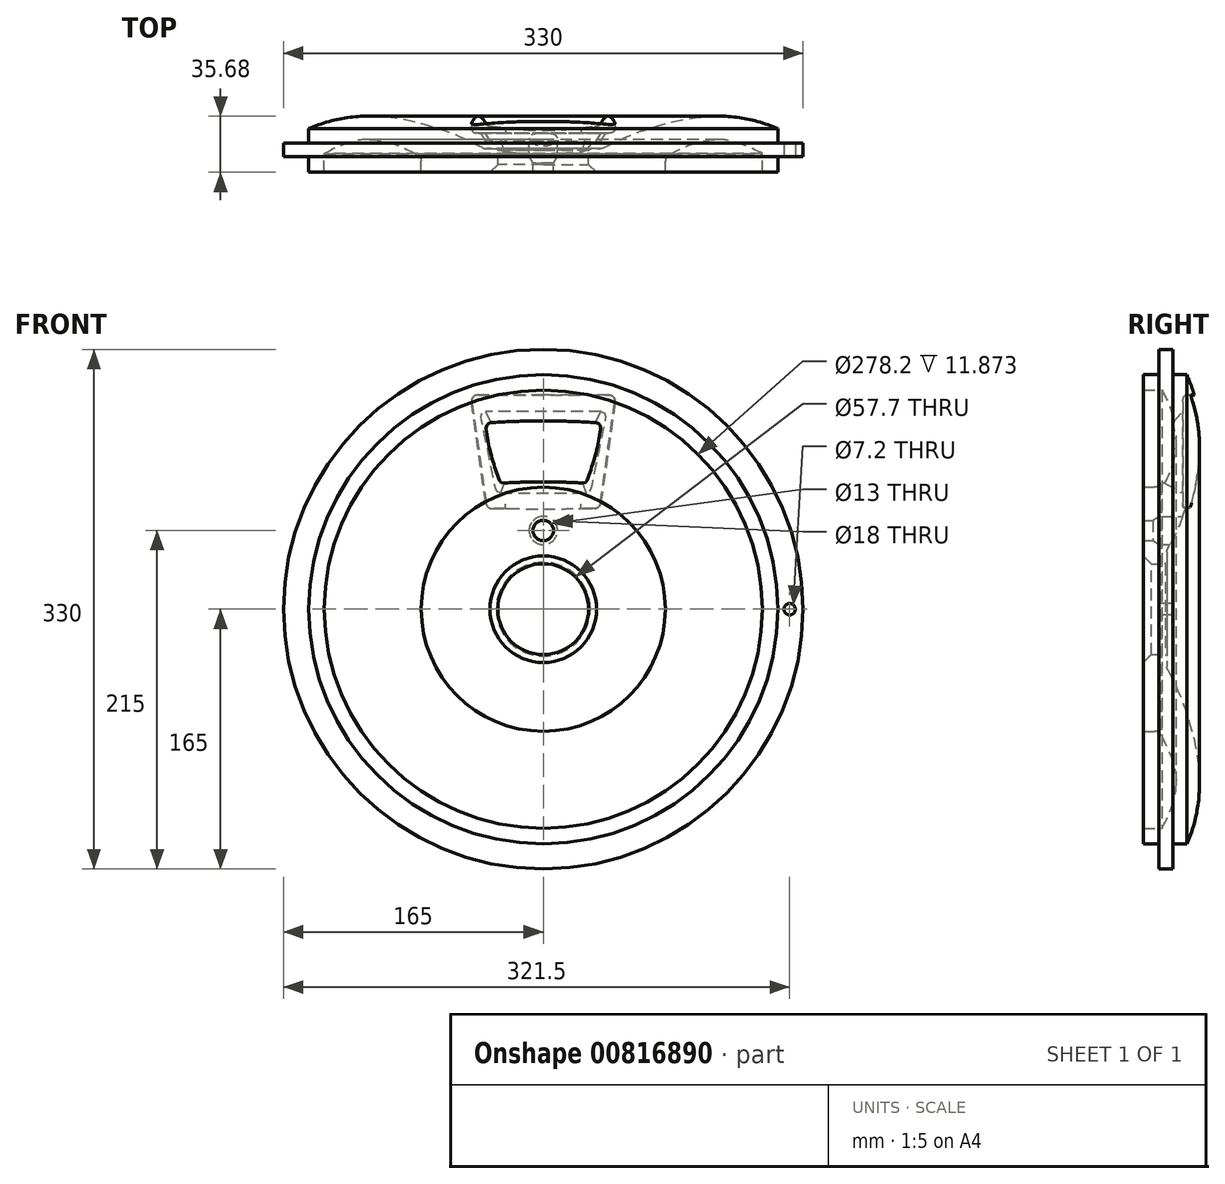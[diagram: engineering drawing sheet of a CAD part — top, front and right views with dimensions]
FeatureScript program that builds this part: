
annotation { "Feature Type Name" : "Feature", "Feature Type Description" : "" }
export const myFeature = defineFeature(function(context is Context, id is Id, definition is map)
    precondition{}
    {
        {
            var Q0;
            Q0=qCreatedBy(makeId("Top.planeOp"),FACE);
            var sketch = newSketch(context, id + "F0", { "sketchPlane" : qUnion([Q0])});
            skLineSegment(sketch, "E0", {"start": v(-28.85, 0) * mm, "end": v(-28.85, 15) * mm});
            skLineSegment(sketch, "E1", {"start": v(-28.85, 15) * mm, "end": v(-36.25, 15) * mm});
            skFitSpline(sketch, "E2", {"points": [v(-37.5, 15) * mm, v(-69.56, 28.6) * mm, v(-105.66, 35.55) * mm, v(-165, 18.67) * mm], "startDerivative": vector(-135.79, 72.9) * mm, "endDerivative": vector(-162.08, -109.99) * mm});
            skLineSegment(sketch, "E3", {"start": v(-165, 10) * mm, "end": v(-149, 10) * mm});
            skLineSegment(sketch, "E4", {"start": v(-149, 10) * mm, "end": v(-149, 0) * mm});
            skLineSegment(sketch, "E5", {"start": v(-149, 0) * mm, "end": v(-139.1, 0) * mm});
            skLineSegment(sketch, "E6", {"start": v(-139.1, 0) * mm, "end": v(-139.1, 11.87) * mm});
            skLineSegment(sketch, "E7", {"start": v(-77.5, 7) * mm, "end": v(-77.5, 0) * mm});
            skLineSegment(sketch, "E8", {"start": v(-77.5, 0) * mm, "end": v(-28.85, 0) * mm});
            skLineSegment(sketch, "E9", {"start": v(0, 47.35) * mm, "end": v(0, -31.33) * mm, "construction": true});
            skFitSpline(sketch, "E10", {"points": [v(-139.1, 11.87) * mm, v(-77.5, 10) * mm], "startDerivative": vector(71.54, 38.93) * mm, "endDerivative": vector(74.78, -40.54) * mm});
            skLineSegment(sketch, "E11", {"start": v(-165, 18.67) * mm, "end": v(-149, 18.67) * mm});
            skLineSegment(sketch, "E12", {"start": v(-149, 18.67) * mm, "end": v(-149, 27.64) * mm});
            skLineSegment(sketch, "E13", {"start": v(-165, 18.67) * mm, "end": v(-165, 10) * mm});
            skArc(sketch, "E14.filletArc", {"start": v(-77.5, 7) * mm, "mid": v(-78.22, 9.59) * mm, "end": v(-80.18, 11.43) * mm});
            skArc(sketch, "E15.filletArc", {"start": v(-38.6, 15.58) * mm, "mid": v(-37.46, 15.15) * mm, "end": v(-36.25, 15) * mm});
            skSolve(sketch);
        }
        {
            var Q0;
            Q0=makeQuery(id+"F0.imprint","IMPRINT",FACE,{"disambiguationData":[TD([[makeQuery(id+"F0.imprint","IMPRINT",EDGE,{"derivedFrom":sQuery(id+"F0.wireOp",EDGE,"E0")}),1.0]])]});
            var Q1;
            Q1=sQuery(id+"F0.wireOp",EDGE,"E9");
            revolve(context, id + "F1", {"surfaceOperationType" : NewSurfaceOperationType.NEW, "entities" : qUnion([Q0]), "axis" : qUnion([Q1]), "revolveType" : RevolveType.FULL});
        }
        {
            var Q0;
            Q0=qCreatedBy(makeId("Front.planeOp"),FACE);
            var sketch = newSketch(context, id + "F2", { "sketchPlane" : qUnion([Q0])});
            skLineSegment(sketch, "E16", {"start": v(22, 96.62) * mm, "end": v(-22, 96.62) * mm});
            skLineSegment(sketch, "E17", {"start": v(-25, 93.62) * mm, "end": v(-25, 90.45) * mm});
            skLineSegment(sketch, "E18", {"start": v(-22, 87.45) * mm, "end": v(22, 87.45) * mm});
            skLineSegment(sketch, "E19", {"start": v(25, 90.45) * mm, "end": v(25, 93.62) * mm});
            skPoint(sketch, "E20.visualSharp", {"position": v(-25, 96.62) * mm});
            skArc(sketch, "E20.filletArc", {"start": v(-22, 96.62) * mm, "mid": v(-24.12, 95.74) * mm, "end": v(-25, 93.62) * mm});
            skPoint(sketch, "E21.visualSharp", {"position": v(-25, 87.45) * mm});
            skArc(sketch, "E21.filletArc", {"start": v(-25, 90.45) * mm, "mid": v(-24.12, 88.33) * mm, "end": v(-22, 87.45) * mm});
            skPoint(sketch, "E22.visualSharp", {"position": v(25, 87.45) * mm});
            skArc(sketch, "E22.filletArc", {"start": v(22, 87.45) * mm, "mid": v(24.12, 88.33) * mm, "end": v(25, 90.45) * mm});
            skPoint(sketch, "E23.visualSharp", {"position": v(25, 96.62) * mm});
            skArc(sketch, "E23.filletArc", {"start": v(25, 93.62) * mm, "mid": v(24.12, 95.74) * mm, "end": v(22, 96.62) * mm});
            skSolve(sketch);
        }
        {
            var Q0;
            Q0=qCreatedBy(makeId("Front.planeOp"),FACE);
            cPlane(context, id + "F3", {"entities" : qUnion([Q0]), "cplaneType" : CPlaneType.OFFSET, "offset" : 50 * mm, "oppositeDirection" : true, "width" : 150 * mm, "height" : 150 * mm});
        }
        {
            var Q0;
            Q0=qCreatedBy(id+"F3.planeOp",FACE);
            var sketch = newSketch(context, id + "F4", { "sketchPlane" : qUnion([Q0])});
            skLineSegment(sketch, "E24", {"start": v(32.57, 59.93) * mm, "end": v(-32.57, 59.93) * mm});
            skLineSegment(sketch, "E25", {"start": v(-51.3, 154.4) * mm, "end": v(51.3, 154.4) * mm});
            skLineSegment(sketch, "E26", {"start": v(35.5, 62.3) * mm, "end": v(54.23, 150.77) * mm});
            skLineSegment(sketch, "E27", {"start": v(-54.23, 150.77) * mm, "end": v(-35.5, 62.3) * mm});
            skPoint(sketch, "E28.visualSharp", {"position": v(55, 154.4) * mm});
            skArc(sketch, "E28.filletArc", {"start": v(54.23, 150.77) * mm, "mid": v(53.63, 153.28) * mm, "end": v(51.3, 154.4) * mm});
            skPoint(sketch, "E29.visualSharp", {"position": v(-55, 154.4) * mm});
            skArc(sketch, "E29.filletArc", {"start": v(-51.3, 154.4) * mm, "mid": v(-53.63, 153.28) * mm, "end": v(-54.23, 150.77) * mm});
            skPoint(sketch, "E30.visualSharp", {"position": v(-35, 59.93) * mm});
            skArc(sketch, "E30.filletArc", {"start": v(-35.5, 62.3) * mm, "mid": v(-34.46, 60.6) * mm, "end": v(-32.57, 59.93) * mm});
            skPoint(sketch, "E31.visualSharp", {"position": v(35, 59.93) * mm});
            skArc(sketch, "E31.filletArc", {"start": v(32.57, 59.93) * mm, "mid": v(34.46, 60.6) * mm, "end": v(35.5, 62.3) * mm});
            skSolve(sketch);
        }
        {
            var Q1;
            Q1 = qSketchRegion(id + "F2", true);
            var Q2;
            Q2 = qSketchRegion(id + "F4", true);
            loft(context, id + "F5", {"operationType" : NewBodyOperationType.REMOVE, "sheetProfilesArray" : [{ "sheetProfileEntities" : qUnion([Q1]) }, { "sheetProfileEntities" : qUnion([Q2]) }]});
        }
        {
            var Q0;
            Q0=qCreatedBy(makeId("Front.planeOp"),FACE);
            var sketch = newSketch(context, id + "F6", { "sketchPlane" : qUnion([Q0])});
            skCircle(sketch, "E32", {"center": v(156.5, 0) * mm, "radius": 3.6 * mm});
            skSolve(sketch);
        }
        {
            var Q0;
            Q0 = qSketchRegion(id + "F6", true);
            extrude(context, id + "F7", {"entities" : qUnion([Q0]), "operationType" : NewBodyOperationType.REMOVE, "oppositeDirection" : true, "depth" : 50 * mm, "offsetDistance" : 25 * mm});
        }
        {
            var Q0;
            Q0=qCreatedBy(makeId("Right.planeOp"),FACE);
            var sketch = newSketch(context, id + "F8", { "sketchPlane" : qUnion([Q0])});
            skLineSegment(sketch, "E33", {"start": v(0, 50) * mm, "end": v(51.06, 50) * mm});
            skLineSegment(sketch, "E34", {"start": v(0, 56.5) * mm, "end": v(6, 56.5) * mm});
            skLineSegment(sketch, "E35", {"start": v(6, 56.5) * mm, "end": v(10.33, 59) * mm});
            skLineSegment(sketch, "E36", {"start": v(10.33, 59) * mm, "end": v(51.06, 59) * mm});
            skLineSegment(sketch, "E37", {"start": v(51.06, 59) * mm, "end": v(51.06, 50) * mm});
            skLineSegment(sketch, "E38", {"start": v(0, 50) * mm, "end": v(0, 56.5) * mm});
            skSolve(sketch);
        }
        {
            var Q0;
            Q0 = qSketchRegion(id + "F8", true);
            var Q1;
            Q1=sQuery(id+"F8.wireOp",EDGE,"E33");
            revolve(context, id + "F9", {"operationType" : NewBodyOperationType.REMOVE, "surfaceOperationType" : NewSurfaceOperationType.NEW, "entities" : qUnion([Q0]), "axis" : qUnion([Q1]), "revolveType" : RevolveType.FULL, "oppositeDirection" : true});
        }
        {
            var Q0;
            Q0=makeQuery(id+"F1.opRevolve","SWEPT_EDGE",EDGE,{"disambiguationData":[OSD([sQuery(id+"F0.wireOp",EDGE,"E0"),sQuery(id+"F0.wireOp",EDGE,"E8")])]});
            chamfer(context, id + "F10", {"entities" : qUnion([Q0]), "width" : 5 * mm, "tangentPropagation" : true});
        }
        {
            var Q0;
            Q0=makeQuery(id+"F1.opRevolve","SWEPT_EDGE",EDGE,{"disambiguationData":[OSD([sQuery(id+"F0.wireOp",EDGE,"E0"),sQuery(id+"F0.wireOp",EDGE,"E1")])]});
            chamfer(context, id + "F11", {"entities" : qUnion([Q0]), "width" : 1 * mm, "tangentPropagation" : true});
        }
        {
            var Q0;
            Q0=qCreatedBy(id+"F3.planeOp",FACE);
            var sketch = newSketch(context, id + "F12", { "sketchPlane" : qUnion([Q0])});
            skLineSegment(sketch, "E39", {"start": v(35.37, 67.58) * mm, "end": v(44.51, 131.58) * mm});
            skLineSegment(sketch, "E40", {"start": v(41.54, 135) * mm, "end": v(-41.54, 135) * mm});
            skLineSegment(sketch, "E41", {"start": v(-44.51, 131.58) * mm, "end": v(-35.37, 67.58) * mm});
            skLineSegment(sketch, "E42", {"start": v(-32.4, 65) * mm, "end": v(32.4, 65) * mm});
            skPoint(sketch, "E43.visualSharp", {"position": v(-45, 135) * mm});
            skArc(sketch, "E43.filletArc", {"start": v(-41.54, 135) * mm, "mid": v(-43.8, 133.97) * mm, "end": v(-44.51, 131.58) * mm});
            skPoint(sketch, "E44.visualSharp", {"position": v(-35, 65) * mm});
            skArc(sketch, "E44.filletArc", {"start": v(-35.37, 67.58) * mm, "mid": v(-34.36, 65.73) * mm, "end": v(-32.4, 65) * mm});
            skPoint(sketch, "E45.visualSharp", {"position": v(35, 65) * mm});
            skArc(sketch, "E45.filletArc", {"start": v(32.4, 65) * mm, "mid": v(34.36, 65.73) * mm, "end": v(35.37, 67.58) * mm});
            skPoint(sketch, "E46.visualSharp", {"position": v(45, 135) * mm});
            skArc(sketch, "E46.filletArc", {"start": v(44.51, 131.58) * mm, "mid": v(43.8, 133.97) * mm, "end": v(41.54, 135) * mm});
            skSolve(sketch);
        }
        {
            var Q0;
            Q0 = qSketchRegion(id + "F12", true);
            extrude(context, id + "F13", {"entities" : qUnion([Q0]), "operationType" : NewBodyOperationType.REMOVE, "depth" : 25 * mm, "offsetDistance" : 25 * mm, "hasDraft" : true, "draftAngle" : 3 * degree});
        }
        {
            var Q0;
            Q0=makeQuery(id+"F13.boolean.opBoolean","COPY",EDGE,{"derivedFrom":makeQuery(id+"F13.opExtrude","CAP_EDGE",EDGE,{"disambiguationData":[OSD([sQuery(id+"F12.wireOp",EDGE,"E40")])],"isStart":false})});
            fillet(context, id + "F14", {"entities" : qUnion([Q0]), "radius" : 3 * mm, "tangentPropagation" : true, "allowEdgeOverflow" : false});
        }
    });
